# Revit family: Bath-Freestanding-KALLISTA-Circle-P50202_1
name_source: partatom
category: Plumbing Fixtures
units: mm (PartAtom-declared; Revit-internal decimal feet)

## family parameters
Cut with Voids When Loaded = No
Host = Face
Maintain Annotation Orientation = No
OmniClass Number = 23.31.15.00
OmniClass Title = Bathtubs
Part Type = Normal
Room Calculation Point = No
Round Connector Dimension = Use Diameter
Shared = No

## types (4) — shared parameters
ADA Compliant = No
Assembly Code = D2010500
CW Connection = No
Cold Water Inlet = Cold Water Inlet
Date Modified = 06/10/2025
Default Elevation = 0"
Drain Included = Yes
HW Connection = No
Height = 20 11/16"
Hot Water Inlet = Hot Water Inlet
Length = 31 1/4"
Manufacturer = Kallista Co.
Master Format 2014 = 22 41 19
Master Format 2014 Name = Residential Bathtubs
Material = Premium Metal Construction
Product Documentation Link = https://techcomm.kohler.com
Product Name = Circle
URL = https://www.kallista.com
Vent Connection = No
Waste Connection = Yes
Waste Water Outlet = Waste Water Outlet
WaterSense Certified = No
Width = 68 11/16"

## per-type parameters (varying)
| type | Description | Finish | Model | Product Page URL | Type |
| 00-8W | Bath No Feet-Exterior | Kallista-Metal-BL-Matte_Black | P50202-00-8W |  | 1 |
| NA-0 | Freestanding Claw Foot Bathtub with Primed Exterior | Kallista-Cast_Iron-NA-Prime | P50202-NA-0 | https://www.kallista.com | 2 |
| P5-0 | Freestanding Claw Foot Bathtub with Black Exterior | Kallista-Cast_Iron-P5-Iron_Black | P50202-P5-0 | https://www.kallista.com | 3 |
| W-0 | Freestanding Claw Foot Bathtub with White Exterior | Kallista-Cast_Iron-0-White | P50202-W-0 | https://www.kallista.com | 4 |

## geometry (parser evidence)
native form markers: Sweep x5
no freeform markers — native parametric forms only
